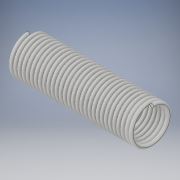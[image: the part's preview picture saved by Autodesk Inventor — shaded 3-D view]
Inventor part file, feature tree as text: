
AUTODESK INVENTOR PART (.ipt)
format: ipt  version: 2018.3 (Build 223284000, 284)  size: 690,176 bytes
history: native  units: in
note: dims shown in document units (in); Inventor stores cm internally (conversion verified against a paired STEP export)
features: helix x1, sketch x1
ambient origin geometry x8: Origin, YZ Plane, XZ Plane, XY Plane, X Axis, Y Axis, Z Axis, Center Point
bodies: Solid1 (feature_tree)
feature tree (2):
  helix  "Coil1"  [1 undecoded]
  sketch  "Sketch1"  dims[d1=0.043in d3=0.215in d4=1.0in d5=1.375in d6=11.811in d7=0.0in d8=90.0deg d9=90.0deg d10=0.0in d11=0.0in]
note: 1 required parameter value undecoded (feature->parameter linkage not recoverable at this tier; creation-order binding heuristic only, values carry confidence <= 0.55)
